# Revit family: Lighting_Pendants_Nordlux_Artist_40
name_source: partatom
category: Lighting Fixtures
revit_build: Autodesk Revit 2017 (Build: 20160225_1515(x64)
units: mm (PartAtom-declared; Revit-internal decimal feet)

## family parameters
Always vertical = Yes
Cut with Voids When Loaded = No
Host = Ceiling
Light Source = Yes
OmniClass Number = 23.80.70.11
OmniClass Title = Luminaries for Internal Lighting
Part Type = Normal
Room Calculation Point = No
Round Connector Dimension = Use Diameter
Shared = No

## types (4) — shared parameters
AssetType = Fixed
BIMObjectName = Lighting_Pendants_Nordlux_Artist_40
Brand = Nordlux
Category = Indoor lighting
Collection = Artist
Color Filter = 16777215
ColourIndexRA = 80
ConvergoRefNr = 0143-1909-0002-DK
Description = With its timeless design and simple shape, ARTIST is a beautiful candidate for a future classic. As the name suggests, Artist is modeled on the world of music – inspired by a drum kit cymbal.
Designer = Bonnelycke MDD
Dimming Lamp Color Temperature Shift = <None>
DurationUnit = Hours
Emit Shape Visible in Rendering = No
Emit from Circle Diameter = 380 mm
EnergyClass = A - A++
ExpectedLife = 20.000
Features = Textile cable 300cm. Cable can not be replaced.
Finish = Primary material metal, secondary material plastic, textile cable.
HasProtectiveEarth = No
IP_Code = IP20
IfcExportAs = IfcLightFixtureType
IfcExportType = NOTDEFINED
InsulationStandardClass = Class 2 (Double isolated)
LensMaterial = Glass
LightFixtureMountingType = Suspended
LightFixturePlacingType = Ceilling
LightSource = Incl. 24W LED
LuminairePowerFactor = 0.98
Manufacturer = Nordlux
ManufacturerName = Nordlux
ManufacturerURL = https://www.nordlux.com
Material = Metal, plastic & textile
NBSDescription = General purpose luminaires
NBSReference = 90-60-50/405
Name = Artist_40
NominalCurrent = 0 A
NominalDiameter = 400 mm  [stored 1.31234 ft]
NominalFrequencyRange = 50 Hz
NominalLength = 400 mm  [stored 1.31234 ft]
NominalRadius = 200 mm  [stored 0.656168 ft]
NominalVoltage = 230 V
NominalVoltageCalc = 0 V
NominalWidth = 400 mm  [stored 1.31234 ft]
NumberOfPoles = 1
PhaseAngle = 0.00°
Photometric Web File = 8309 Artist 40.ies
Product data url = https://www.bimobject.com
Revision = 1
Shape = Sculptured
Size = Shade: 400x400x60 mm / Canopy: 114x114x82 mm
Socket = LED MODUL
Tilt Angle = 90.00°
TotalWattage = 24 W
URL = https://www.nordlux.com
Uniclass2 = Pr_70_70_49_86
Uniclass2015Description = Pendant  luminaires
Uniclass2015Reference = Pr_70_70_48_62
UsageCurrent = 0 A
Version = 1
VersionDate = 01/07/2020
WarrantyDurationUnit = Hours
zero-valued in all types: DefaultElevation, ElectricalDeviceNominalPower, MaintenanceFactor, NumberOfSources

## per-type parameters (varying)
| type | ArticleNumber | Color | EANNumber | LightFixtureMainMaterial | LightFixtureSecondaryMaterial | ModelReference |
| Artist 40 - black | 83093003 | Black | 5701581345584 | Black | Black cable | 83093003 |
| Artist 40 - grey | 83093010 | Grey | 5701581301283 | Grey | Grey cable | 83093010 |
| Artist 40 - copper | 83093030 | Copper | 5701581301382 | Copper | Black cable | 83093030 |
| Artist 40 - silver | 83093054 | Silver | 5701581386983 | Silver | Black cable | 83093054 |

note: column(s) folded — value = type name in every type: Model

note: [stored X ft] marks values corroborated as IEEE doubles in the binary element streams (Revit-internal decimal feet)

## geometry (parser evidence)
native form markers: Sweep x8
no freeform markers — native parametric forms only
